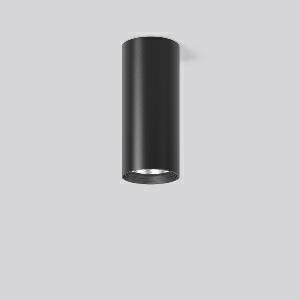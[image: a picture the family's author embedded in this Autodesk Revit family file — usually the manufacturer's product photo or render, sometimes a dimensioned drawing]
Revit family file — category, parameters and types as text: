
# Revit family: heledon_mini_a_931210_003_1_76_a3bb
name_source: partatom
category: Lighting Fixtures
units: mm (PartAtom-declared; Revit-internal decimal feet)

## family parameters
Cut with Voids When Loaded = No
Host = Face
Light Source = No
Part Type = Normal
Room Calculation Point = No
Round Connector Dimension = Use Diameter
Shared = No

## types (1)
- HELEDON mini A (1 x LED Modul 940, 3900 lm, 4000)
    Apparent Load = 29 VA
    Approval mark = CE
    CIE Flux Codes = 95 99 100 100 100
    Color Rendering = 92
    Color Temperature = 4000
    Default Elevation = 1800 mm
    Description = Series: HELEDON mini
Cylindrical surface-mounted downlight. Housing: die-cast aluminium, powder-coated. Internal ceiling frame polycarbonate with bayonet mounting. Black plastic ring and recessed LED to prevent glare from the side. Optical assembly with reflector made of MIRO-Silver with 98% total light reflection for outstanding efficiency - can be changed without tools. Best colour rendering index Ra>90. Suitable for Ceiling mounting. Easy installation with a separate ceiling frame with bayonet mounting and plug connection. Driver integrated. Connected via plug-in connector. High quality converter without flickering and stroboscopic effect. The following accessories can be mounted without use of tools: interchangeable lenses, decorative glasses, honeycomb louvre, clear and frosted diffusers, white interchangeable plastic ring. 
Colour: deep black, matt (RAL 9005)
Diameter: 87 mm
Height: 197 mm
Lamp: LED
Socket: without socket
Colour temperature: 4000K
Colour rendering index (CRI): 92
System power: 29 W
Rated luminous flux: 3900 lm
Luminous efficiency: 134 lm/W
Control gear: Converter, dimmable, DALI
Protection class: I
Type of protection: IP 20
    Height = 197 mm
    Lamp = 1 x LED Modul 940
    Lamp Light Flux = 3900 lm
    Lamp count = 1
    Length = 87 mm
    Lifetime = 50000 h
    Luminous efficacy = 134 lm/W
    Manufacturer = RZB
    ModVariant = No
    Model = 931210.003.1.76
    Mounting Place = Ceiling
    Mounting Type = Surface mounted
    Number of Poles = 1
    OnlyDefault = Yes
    Power Factor = 1
    Product Name = HELEDON mini A
    Product group = Surface mounted downlights
    ProductGroupID = 302
    Protection Class = Protection class I
    Protection Degree = IP 20
    RLX_Detail_Level = 1
    RLX_Emergency_Light_Flux = 0 lm
    RLX_Emergency_Type = 0
    RLX_Emergency_Type_DB = No
    RlxData = <blob elided: 107685 chars, md5=55163721>
    Socket = socket
    Standby Power = 0 W
    System Light Flux = 3900 lm
    System Power = 29 W
    Type Comments = Product without accessories
    Type Image = 931188.003.jpg
    URL = http://relux.com
    VarID = ---
    Voltage = 230 V
    Voltage Range = 220-240 V
    Weight = 0.00 kg
    Width = 0 mm  [stored 0 ft]

note: [stored X ft] marks values corroborated as IEEE doubles in the binary element streams (Revit-internal decimal feet)

## geometry (parser evidence)
native form markers: Blend x4, Sweep x9
no freeform markers — native parametric forms only
